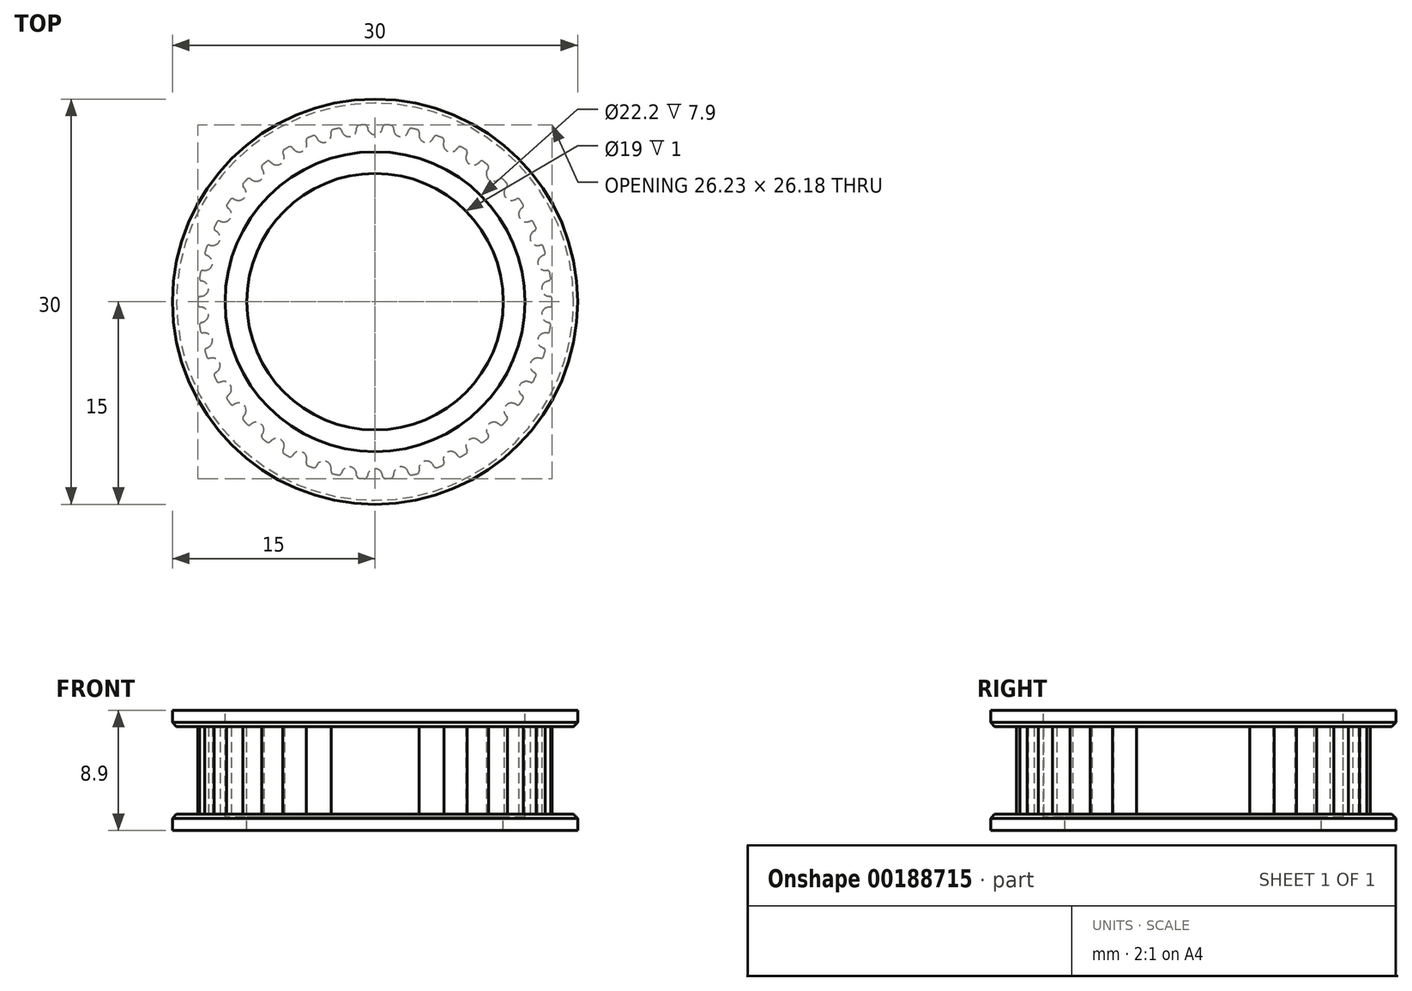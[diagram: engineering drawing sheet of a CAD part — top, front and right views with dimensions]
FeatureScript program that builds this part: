
annotation { "Feature Type Name" : "Feature", "Feature Type Description" : "" }
export const myFeature = defineFeature(function(context is Context, id is Id, definition is map)
    precondition{}
    {
        {
            assignVariable(context, id + "F0", {"name" : "teeth", "anyValue" : 42});
        }
        {
            assignVariable(context, id + "F1", {"name" : "belt_width", "anyValue" : 6.5});
        }
        {
            var Q0;
            Q0=qCreatedBy(makeId("Top.planeOp"),FACE);
            var sketch = newSketch(context, id + "F2", { "sketchPlane" : qUnion([Q0])});
            skLineSegment(sketch, "E0", {"start": v(0, 0) * mm, "end": v(0, 12.37) * mm, "construction": true});
            skCircle(sketch, "E1", {"center": v(0, 0) * mm, "radius": 13.12 * mm});
            skPoint(sketch, "E2.MirrorCS.end.orphan", {"position": v(0.98, 13.08) * mm});
            skLineSegment(sketch, "E3", {"start": v(0.98, 13.08) * mm, "end": v(1, 13.33) * mm, "construction": true});
            skLineSegment(sketch, "E4", {"start": v(-0.98, 13.08) * mm, "end": v(-1, 13.33) * mm, "construction": true});
            skArc(sketch, "E5", {"start": v(0, 12.37) * mm, "mid": v(0.34, 12.48) * mm, "end": v(0.54, 12.77) * mm});
            skArc(sketch, "E6", {"start": v(0.54, 12.77) * mm, "mid": v(0.56, 12.87) * mm, "end": v(0.58, 12.97) * mm, "construction": true});
            skLineSegment(sketch, "E7", {"start": v(0, 12.37) * mm, "end": v(0, 13.12) * mm, "construction": true});
            skLineSegment(sketch, "E8", {"start": v(0, 13.12) * mm, "end": v(0, 13.37) * mm, "construction": true});
            skArc(sketch, "E9", {"start": v(0.58, 12.97) * mm, "mid": v(0.64, 13.06) * mm, "end": v(0.74, 13.1) * mm, "construction": true});
            skArc(sketch, "E10", {"start": v(1, 13.33) * mm, "mid": v(0, 13.37) * mm, "end": v(-1, 13.33) * mm, "construction": true});
            skLineSegment(sketch, "E11", {"start": v(0.98, 13.08) * mm, "end": v(0.92, 12.33) * mm});
            skLineSegment(sketch, "E12", {"start": v(0.92, 12.33) * mm, "end": v(0, 0) * mm});
            skLineSegment(sketch, "E13", {"start": v(0, 0) * mm, "end": v(-0.92, 12.33) * mm});
            skLineSegment(sketch, "E14", {"start": v(-0.92, 12.33) * mm, "end": v(-0.98, 13.08) * mm});
            skArc(sketch, "E15", {"start": v(0.77, 13.1) * mm, "mid": v(0.65, 13.06) * mm, "end": v(0.58, 12.95) * mm});
            skArc(sketch, "E16", {"start": v(0.54, 12.77) * mm, "mid": v(0.56, 12.86) * mm, "end": v(0.58, 12.95) * mm});
            skArc(sketch, "E17.MirrorCS", {"start": v(0, 12.37) * mm, "mid": v(-0.34, 12.48) * mm, "end": v(-0.54, 12.77) * mm});
            skArc(sketch, "E18.MirrorCS", {"start": v(-0.54, 12.77) * mm, "mid": v(-0.56, 12.86) * mm, "end": v(-0.58, 12.95) * mm});
            skArc(sketch, "E19.MirrorCS", {"start": v(-0.77, 13.1) * mm, "mid": v(-0.65, 13.06) * mm, "end": v(-0.58, 12.95) * mm});
            skArc(sketch, "E20", {"start": v(0, 13.12) * mm, "mid": v(-0.2, 13.11) * mm, "end": v(-0.4, 13.1) * mm});
            skArc(sketch, "E21", {"start": v(0.92, 12.33) * mm, "mid": v(0, 12.37) * mm, "end": v(-0.92, 12.33) * mm, "construction": true});
            skLineSegment(sketch, "E22", {"start": v(1, 13.33) * mm, "end": v(1.03, 13.7) * mm, "construction": true});
            skLineSegment(sketch, "E23", {"start": v(-1, 13.33) * mm, "end": v(-1.03, 13.7) * mm, "construction": true});
            skArc(sketch, "E24", {"start": v(-1.03, 13.7) * mm, "mid": v(0, 13.75) * mm, "end": v(1.03, 13.7) * mm, "construction": true});
            skSolve(sketch);
        }
        {
            var Q0;
            Q0=makeQuery(id+"F2.imprint","IMPRINT",FACE,{"disambiguationData":[TD([[makeQuery(id+"F2.imprint","IMPRINT",EDGE,{"derivedFrom":sQuery(id+"F2.wireOp",EDGE,"E5")}),-1.0]])]});
            var Q1;
            {var subQ1=sQuery(id+"F2.wireOp",EDGE,"E14");Q1=makeQuery(id+"F2.imprint","IMPRINT",FACE,{"disambiguationData":[TD([[makeQuery(id+"F2.imprint","IMPRINT",EDGE,{"derivedFrom":subQ1}),-1.0]])]});}
            var Q2;
            {var subQ0=sQuery(id+"F2.wireOp",EDGE,"E12");Q2=makeQuery(id+"F2.imprint","IMPRINT",FACE,{"disambiguationData":[TD([[makeQuery(id+"F2.imprint","IMPRINT",EDGE,{"derivedFrom":subQ0}),-1.0]])]});}
            extrude(context, id + "F3", {"entities" : qUnion([Q0, Q1, Q2]), "depth" : (getVariable(context, 'belt_width')) * mm, "symmetric" : true});
        }
        {
            var Q0;
            Q0=makeQuery(id+"F3.opExtrude","SWEPT_BODY",BODY,{"disambiguationData":[OSD([sQuery(id+"F2.wireOp",EDGE,"E1"),sQuery(id+"F2.wireOp",EDGE,"E5"),sQuery(id+"F2.wireOp",EDGE,"E11"),sQuery(id+"F2.wireOp",EDGE,"E12"),sQuery(id+"F2.wireOp",EDGE,"E13"),sQuery(id+"F2.wireOp",EDGE,"E14"),sQuery(id+"F2.wireOp",EDGE,"E15"),sQuery(id+"F2.wireOp",EDGE,"E16"),sQuery(id+"F2.wireOp",EDGE,"E17.MirrorCS"),sQuery(id+"F2.wireOp",EDGE,"E18.MirrorCS"),sQuery(id+"F2.wireOp",EDGE,"E19.MirrorCS")])]});
            var Q1;
            Q1=makeQuery(id+"F3.opExtrude","SWEPT_EDGE",EDGE,{"disambiguationData":[OSD([sQuery(id+"F2.wireOp",EDGE,"E12"),sQuery(id+"F2.wireOp",EDGE,"E13")])]});
            circularPattern(context, id + "F4", {"operationType" : NewBodyOperationType.ADD, "entities" : qUnion([Q0]), "axis" : qUnion([Q1]), "angle" : 360 * degree, "instanceCount" : getVariable(context, 'teeth'), "equalSpace" : true, "computeTransformsWithoutBuiltin" : true});
        }
        {
            var Q0;
            Q0=qCreatedBy(makeId("Front.planeOp"),FACE);
            var sketch = newSketch(context, id + "F5", { "sketchPlane" : qUnion([Q0])});
            skLineSegment(sketch, "E25", {"start": v(0, -3.25) * mm, "end": v(13.12, -3.25) * mm});
            skLineSegment(sketch, "E26", {"start": v(13.12, -3.25) * mm, "end": v(15, -3.25) * mm});
            skLineSegment(sketch, "E27", {"start": v(0, 3.25) * mm, "end": v(13.12, 3.25) * mm});
            skLineSegment(sketch, "E28", {"start": v(15, 3.25) * mm, "end": v(13.12, 3.25) * mm});
            skLineSegment(sketch, "E29", {"start": v(15, 3.25) * mm, "end": v(15, 4.45) * mm});
            skLineSegment(sketch, "E30", {"start": v(15, 4.45) * mm, "end": v(0, 4.45) * mm});
            skLineSegment(sketch, "E31", {"start": v(0, 4.45) * mm, "end": v(0, 3.25) * mm});
            skLineSegment(sketch, "E32", {"start": v(13.12, 0) * mm, "end": v(13.12, -3.25) * mm, "construction": true});
            skLineSegment(sketch, "E33", {"start": v(15, -4.45) * mm, "end": v(0, -4.45) * mm});
            skLineSegment(sketch, "E34", {"start": v(15, -3.25) * mm, "end": v(15, -4.45) * mm});
            skLineSegment(sketch, "E35", {"start": v(0, -3.25) * mm, "end": v(0, -4.45) * mm});
            skLineSegment(sketch, "E36", {"start": v(0, 4.45) * mm, "end": v(0, -4.45) * mm, "construction": true});
            skSolve(sketch);
        }
        {
            var Q0;
            Q0=makeQuery(id+"F5.imprint","IMPRINT",FACE,{"disambiguationData":[TD([[makeQuery(id+"F5.imprint","IMPRINT",EDGE,{"derivedFrom":sQuery(id+"F5.wireOp",EDGE,"E25")}),-1.0]])]});
            var Q1;
            Q1=makeQuery(id+"F5.imprint","IMPRINT",FACE,{"disambiguationData":[TD([[makeQuery(id+"F5.imprint","IMPRINT",EDGE,{"derivedFrom":sQuery(id+"F5.wireOp",EDGE,"E27")}),1.0]])]});
            var Q2;
            Q2=qConstructionFilter(qBodyType(qCreatedBy(id+"F5",EDGE),BodyType.WIRE),ConstructionObject.NO);
            var Q3;
            Q3=sQuery(id+"F5.wireOp",EDGE,"E36");
            revolve(context, id + "F6", {"operationType" : NewBodyOperationType.ADD, "entities" : qUnion([Q0, Q1]), "surfaceEntities" : qUnion([Q2]), "axis" : qUnion([Q3]), "revolveType" : RevolveType.FULL});
        }
        {
            var Q0;
            Q0=makeQuery(id+"F6.opRevolve","SWEPT_FACE",FACE,{"disambiguationData":[OSD([sQuery(id+"F5.wireOp",EDGE,"E30")])]});
            var sketch = newSketch(context, id + "F7", { "sketchPlane" : qUnion([Q0])});
            skPoint(sketch, "E37", {"position": v(0, 0) * mm});
            skCircle(sketch, "E38", {"center": v(0, 0) * mm, "radius": 11.1 * mm});
            skCircle(sketch, "E39", {"center": v(0, 0) * mm, "radius": 9.5 * mm});
            skSolve(sketch);
        }
        {
            var Q0;
            Q0=makeQuery(id+"F7.imprint","IMPRINT",FACE,{"disambiguationData":[TD([[makeQuery(id+"F7.imprint","IMPRINT",EDGE,{"derivedFrom":sQuery(id+"F7.wireOp",EDGE,"E38")}),1.0]])]});
            extrude(context, id + "F8", {"entities" : qUnion([Q0]), "operationType" : NewBodyOperationType.REMOVE, "oppositeDirection" : true, "depth" : 7.9 * mm});
        }
        {
            var Q0;
            Q0=makeQuery(id+"F8.boolean.opBoolean","SPLIT",FACE,{"disambiguationData":[TD([makeQuery(id+"F8.opExtrude","SWEPT_FACE",FACE,{"disambiguationData":[OSD([sQuery(id+"F7.wireOp",EDGE,"E39")])]})])],"derivedFrom":makeQuery(id+"F6.opRevolve","SWEPT_FACE",FACE,{"disambiguationData":[OSD([sQuery(id+"F5.wireOp",EDGE,"E30")])]})});
            extrude(context, id + "F9", {"entities" : qUnion([Q0]), "operationType" : NewBodyOperationType.REMOVE, "endBound" : BoundingType.UP_TO_NEXT, "oppositeDirection" : true, "depth" : 25 * mm});
        }
        {
            var Q0;
            Q0=makeQuery(id+"F6.opRevolve","SWEPT_EDGE",EDGE,{"disambiguationData":[OSD([sQuery(id+"F5.wireOp",EDGE,"E26"),sQuery(id+"F5.wireOp",EDGE,"E34")])]});
            var Q1;
            Q1=makeQuery(id+"F6.opRevolve","SWEPT_EDGE",EDGE,{"disambiguationData":[OSD([sQuery(id+"F5.wireOp",EDGE,"E28"),sQuery(id+"F5.wireOp",EDGE,"E29")])]});
            chamfer(context, id + "F10", {"entities" : qUnion([Q0, Q1]), "width" : .3 * mm, "tangentPropagation" : true});
        }
    });
